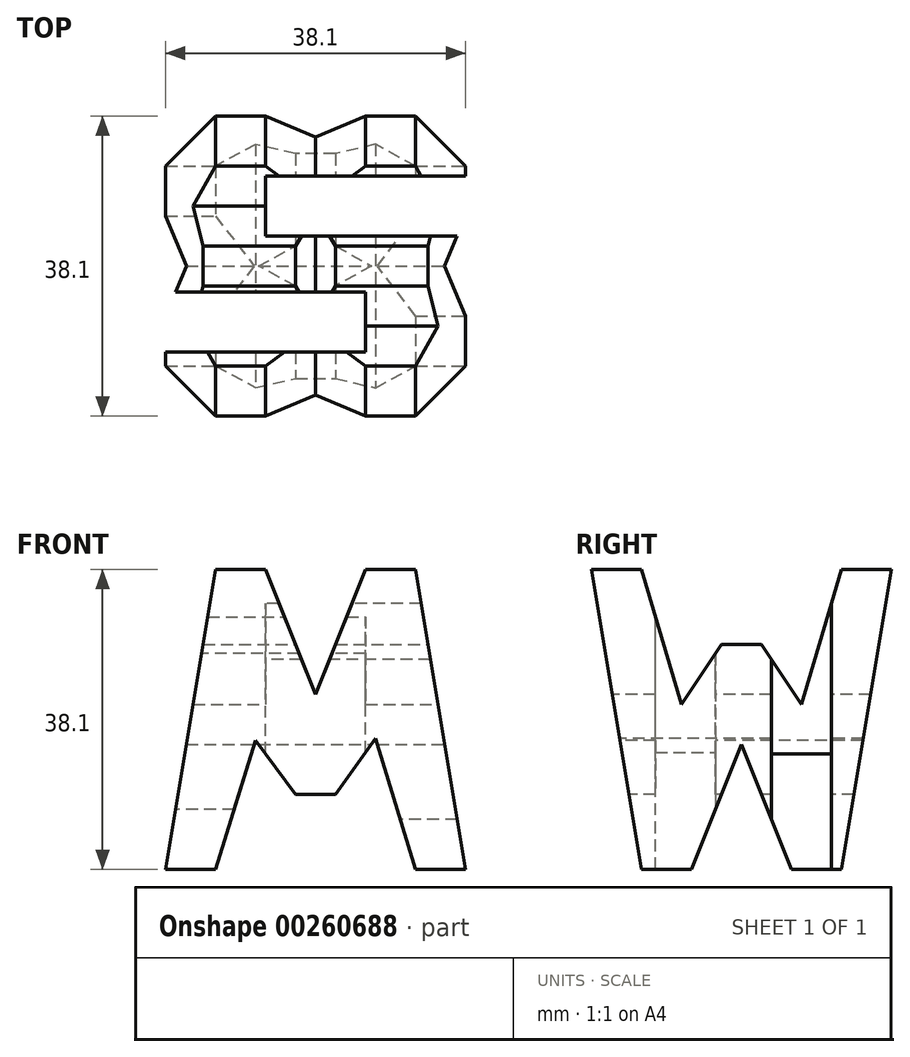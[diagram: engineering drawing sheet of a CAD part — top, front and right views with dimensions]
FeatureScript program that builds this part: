
annotation { "Feature Type Name" : "Feature", "Feature Type Description" : "" }
export const myFeature = defineFeature(function(context is Context, id is Id, definition is map)
    precondition{}
    {
        {
            var Q0;
            Q0=qCreatedBy(makeId("Front.planeOp"),FACE);
            var sketch = newSketch(context, id + "F0", { "sketchPlane" : qUnion([Q0])});
            skPoint(sketch, "E0.end.orphan", {"position": v(-6.42, 11.43) * mm});
            skPoint(sketch, "E1.end.orphan", {"position": v(-6.42, 31.48) * mm});
            skLineSegment(sketch, "E2", {"start": v(0, 0) * mm, "end": v(38.1, 0) * mm});
            skLineSegment(sketch, "E3", {"start": v(38.1, 0) * mm, "end": v(38.1, 38.1) * mm});
            skLineSegment(sketch, "E4", {"start": v(38.1, 38.1) * mm, "end": v(0, 38.1) * mm});
            skLineSegment(sketch, "E5", {"start": v(0, 38.1) * mm, "end": v(0, 0) * mm});
            skSolve(sketch);
        }
        {
            var Q0;
            Q0=qCreatedBy(makeId("Front.planeOp"),FACE);
            cPlane(context, id + "F1", {"entities" : qUnion([Q0]), "cplaneType" : CPlaneType.OFFSET, "offset" : 38.1 * mm, "width" : 152.4 * mm, "height" : 152.4 * mm});
        }
        {
            var Q0;
            Q0 = qSketchRegion(id + "F0", true);
            extrude(context, id + "F2", {"entities" : qUnion([Q0]), "depth" : 38.1 * mm});
        }
        {
            var Q0;
            Q0=qCreatedBy(makeId("Right.planeOp"),FACE);
            cPlane(context, id + "F3", {"entities" : qUnion([Q0]), "cplaneType" : CPlaneType.OFFSET, "offset" : 38.1 * mm, "width" : 152.4 * mm, "height" : 152.4 * mm});
        }
        {
            var Q0;
            Q0=qCreatedBy(makeId("Top.planeOp"),FACE);
            cPlane(context, id + "F4", {"entities" : qUnion([Q0]), "cplaneType" : CPlaneType.OFFSET, "offset" : 38.1 * mm, "width" : 152.4 * mm, "height" : 152.4 * mm});
        }
        {
            var Q0;
            Q0=qCreatedBy(id+"F3.planeOp",FACE);
            var sketch = newSketch(context, id + "F5", { "sketchPlane" : qUnion([Q0])});
            skLineSegment(sketch, "E6", {"start": v(-38.1, 38.1) * mm, "end": v(-31.75, 38.1) * mm});
            skLineSegment(sketch, "E7", {"start": v(-38.1, 38.1) * mm, "end": v(-31.75, 0) * mm});
            skLineSegment(sketch, "E8", {"start": v(-31.75, 0) * mm, "end": v(-25.4, 0) * mm});
            skLineSegment(sketch, "E9", {"start": v(-12.7, 0) * mm, "end": v(-6.35, 0) * mm});
            skLineSegment(sketch, "E10", {"start": v(-6.35, 0) * mm, "end": v(0, 38.1) * mm});
            skLineSegment(sketch, "E11", {"start": v(0, 38.1) * mm, "end": v(-6.35, 38.1) * mm});
            skLineSegment(sketch, "E12.bottom", {"start": v(0, 0) * mm, "end": v(-38.1, 0) * mm});
            skLineSegment(sketch, "E12.top", {"start": v(0, 38.1) * mm, "end": v(-38.1, 38.1) * mm});
            skLineSegment(sketch, "E12.left", {"start": v(0, 0) * mm, "end": v(0, 38.1) * mm});
            skLineSegment(sketch, "E12.right", {"start": v(-38.1, 0) * mm, "end": v(-38.1, 38.1) * mm});
            skLineSegment(sketch, "E13", {"start": v(-25.4, 0) * mm, "end": v(-19.05, 15.87) * mm});
            skPoint(sketch, "E13.endSnap0", {"position": v(-19.05, 0) * mm});
            skLineSegment(sketch, "E14", {"start": v(-19.05, 15.87) * mm, "end": v(-12.7, 0) * mm});
            skPoint(sketch, "E15.start.orphan", {"position": v(-16.51, 33.46) * mm});
            skLineSegment(sketch, "E16", {"start": v(-6.35, 38.1) * mm, "end": v(-11.43, 20.95) * mm});
            skPoint(sketch, "E17.end.orphan", {"position": v(-16.51, 25.49) * mm});
            skLineSegment(sketch, "E18", {"start": v(-26.67, 20.95) * mm, "end": v(-21.59, 28.58) * mm});
            skLineSegment(sketch, "E19", {"start": v(-16.51, 28.57) * mm, "end": v(-21.6, 28.57) * mm});
            skLineSegment(sketch, "E20", {"start": v(-16.51, 28.57) * mm, "end": v(-11.43, 20.95) * mm});
            skPoint(sketch, "E21.end.orphan", {"position": v(-31.53, 33.46) * mm});
            skLineSegment(sketch, "E22", {"start": v(-31.75, 38.1) * mm, "end": v(-26.67, 20.95) * mm});
            skSolve(sketch);
        }
        {
            var Q0;
            {var subQ0=sQuery(id+"F5.wireOp",EDGE,"E16");Q0=makeQuery(id+"F5.imprint","IMPRINT",FACE,{"disambiguationData":[TD([[makeQuery(id+"F5.imprint","IMPRINT",EDGE,{"derivedFrom":subQ0}),-1.0]])]});}
            var Q1;
            {var subQ0=sQuery(id+"F5.wireOp",EDGE,"E10");Q1=makeQuery(id+"F5.imprint","IMPRINT",FACE,{"disambiguationData":[TD([[makeQuery(id+"F5.imprint","IMPRINT",EDGE,{"derivedFrom":subQ0}),-1.0]])]});}
            var Q2;
            {var subQ0=sQuery(id+"F5.wireOp",EDGE,"E13");Q2=makeQuery(id+"F5.imprint","IMPRINT",FACE,{"disambiguationData":[TD([[makeQuery(id+"F5.imprint","IMPRINT",EDGE,{"derivedFrom":subQ0}),-1.0]])]});}
            var Q3;
            {var subQ0=sQuery(id+"F5.wireOp",EDGE,"E7");Q3=makeQuery(id+"F5.imprint","IMPRINT",FACE,{"disambiguationData":[TD([[makeQuery(id+"F5.imprint","IMPRINT",EDGE,{"derivedFrom":subQ0}),-1.0]])]});}
            extrude(context, id + "F6", {"entities" : qUnion([Q0, Q1, Q2, Q3]), "operationType" : NewBodyOperationType.REMOVE, "oppositeDirection" : true, "depth" : 38.1 * mm});
        }
        {
            var Q0;
            Q0=qCreatedBy(id+"F1.planeOp",FACE);
            var sketch = newSketch(context, id + "F7", { "sketchPlane" : qUnion([Q0])});
            skLineSegment(sketch, "E23", {"start": v(6.35, 0) * mm, "end": v(11.43, 16.4) * mm});
            skLineSegment(sketch, "E24", {"start": v(11.43, 16.4) * mm, "end": v(16.51, 9.53) * mm});
            skLineSegment(sketch, "E25", {"start": v(16.51, 9.53) * mm, "end": v(21.6, 9.53) * mm});
            skLineSegment(sketch, "E26", {"start": v(21.6, 9.53) * mm, "end": v(26.67, 16.63) * mm});
            skLineSegment(sketch, "E27", {"start": v(26.67, 16.63) * mm, "end": v(31.75, 0) * mm});
            skLineSegment(sketch, "E28", {"start": v(0, 0) * mm, "end": v(6.35, 38.1) * mm});
            skLineSegment(sketch, "E29", {"start": v(12.7, 38.1) * mm, "end": v(19.05, 22.22) * mm});
            skLineSegment(sketch, "E30", {"start": v(19.05, 22.23) * mm, "end": v(25.4, 38.1) * mm});
            skLineSegment(sketch, "E31", {"start": v(38.1, 0) * mm, "end": v(31.75, 38.1) * mm});
            skLineSegment(sketch, "E32.bottom", {"start": v(0, 0) * mm, "end": v(38.1, 0) * mm});
            skLineSegment(sketch, "E32.top", {"start": v(0, 38.1) * mm, "end": v(38.1, 38.1) * mm});
            skLineSegment(sketch, "E32.left", {"start": v(0, 0) * mm, "end": v(0, 38.1) * mm});
            skLineSegment(sketch, "E32.right", {"start": v(38.1, 0) * mm, "end": v(38.1, 38.1) * mm});
            skSolve(sketch);
        }
        {
            var Q0;
            {var subQ0=sQuery(id+"F7.wireOp",EDGE,"E28");Q0=makeQuery(id+"F7.imprint","IMPRINT",FACE,{"disambiguationData":[TD([[makeQuery(id+"F7.imprint","IMPRINT",EDGE,{"derivedFrom":subQ0}),1.0]])]});}
            var Q1;
            {var subQ0=sQuery(id+"F7.wireOp",EDGE,"E23");Q1=makeQuery(id+"F7.imprint","IMPRINT",FACE,{"disambiguationData":[TD([[makeQuery(id+"F7.imprint","IMPRINT",EDGE,{"derivedFrom":subQ0}),-1.0]])]});}
            var Q2;
            {var subQ0=sQuery(id+"F7.wireOp",EDGE,"E29");Q2=makeQuery(id+"F7.imprint","IMPRINT",FACE,{"disambiguationData":[TD([[makeQuery(id+"F7.imprint","IMPRINT",EDGE,{"derivedFrom":subQ0}),1.0]])]});}
            var Q3;
            {var subQ0=sQuery(id+"F7.wireOp",EDGE,"E31");Q3=makeQuery(id+"F7.imprint","IMPRINT",FACE,{"disambiguationData":[TD([[makeQuery(id+"F7.imprint","IMPRINT",EDGE,{"derivedFrom":subQ0}),-1.0]])]});}
            extrude(context, id + "F8", {"entities" : qUnion([Q0, Q1, Q2, Q3]), "operationType" : NewBodyOperationType.REMOVE, "oppositeDirection" : true, "depth" : 38.1 * mm});
        }
        {
            var Q0;
            Q0=qCreatedBy(id+"F4.planeOp",FACE);
            var sketch = newSketch(context, id + "F9", { "sketchPlane" : qUnion([Q0])});
            skLineSegment(sketch, "E33", {"start": v(0, 0) * mm, "end": v(38.1, 0) * mm});
            skLineSegment(sketch, "E34", {"start": v(38.1, 0) * mm, "end": v(38.1, -38.1) * mm});
            skLineSegment(sketch, "E35", {"start": v(0, 0) * mm, "end": v(0, -38.1) * mm});
            skLineSegment(sketch, "E36", {"start": v(0, -38.1) * mm, "end": v(38.1, -38.1) * mm});
            skLineSegment(sketch, "E37", {"start": v(38.1, -7.62) * mm, "end": v(12.7, -7.62) * mm});
            skLineSegment(sketch, "E38", {"start": v(12.7, -7.62) * mm, "end": v(12.7, -15.24) * mm});
            skLineSegment(sketch, "E39", {"start": v(12.7, -15.24) * mm, "end": v(38.1, -15.24) * mm});
            skLineSegment(sketch, "E40", {"start": v(0, -22.35) * mm, "end": v(25.4, -22.35) * mm});
            skLineSegment(sketch, "E41", {"start": v(25.4, -22.35) * mm, "end": v(25.4, -29.97) * mm});
            skLineSegment(sketch, "E42", {"start": v(25.4, -29.97) * mm, "end": v(1.78, -29.97) * mm});
            skLineSegment(sketch, "E43", {"start": v(1.78, -29.97) * mm, "end": v(0, -29.97) * mm});
            skSolve(sketch);
        }
        {
            var Q0;
            {var subQ0=sQuery(id+"F9.wireOp",EDGE,"E37");Q0=makeQuery(id+"F9.imprint","IMPRINT",FACE,{"disambiguationData":[TD([[makeQuery(id+"F9.imprint","IMPRINT",EDGE,{"derivedFrom":subQ0}),1.0]])]});}
            var Q1;
            {var subQ0=sQuery(id+"F9.wireOp",EDGE,"E40");Q1=makeQuery(id+"F9.imprint","IMPRINT",FACE,{"disambiguationData":[TD([[makeQuery(id+"F9.imprint","IMPRINT",EDGE,{"derivedFrom":subQ0}),-1.0]])]});}
            extrude(context, id + "F10", {"entities" : qUnion([Q0, Q1]), "operationType" : NewBodyOperationType.REMOVE, "oppositeDirection" : true, "depth" : 38.1 * mm});
        }
    });
